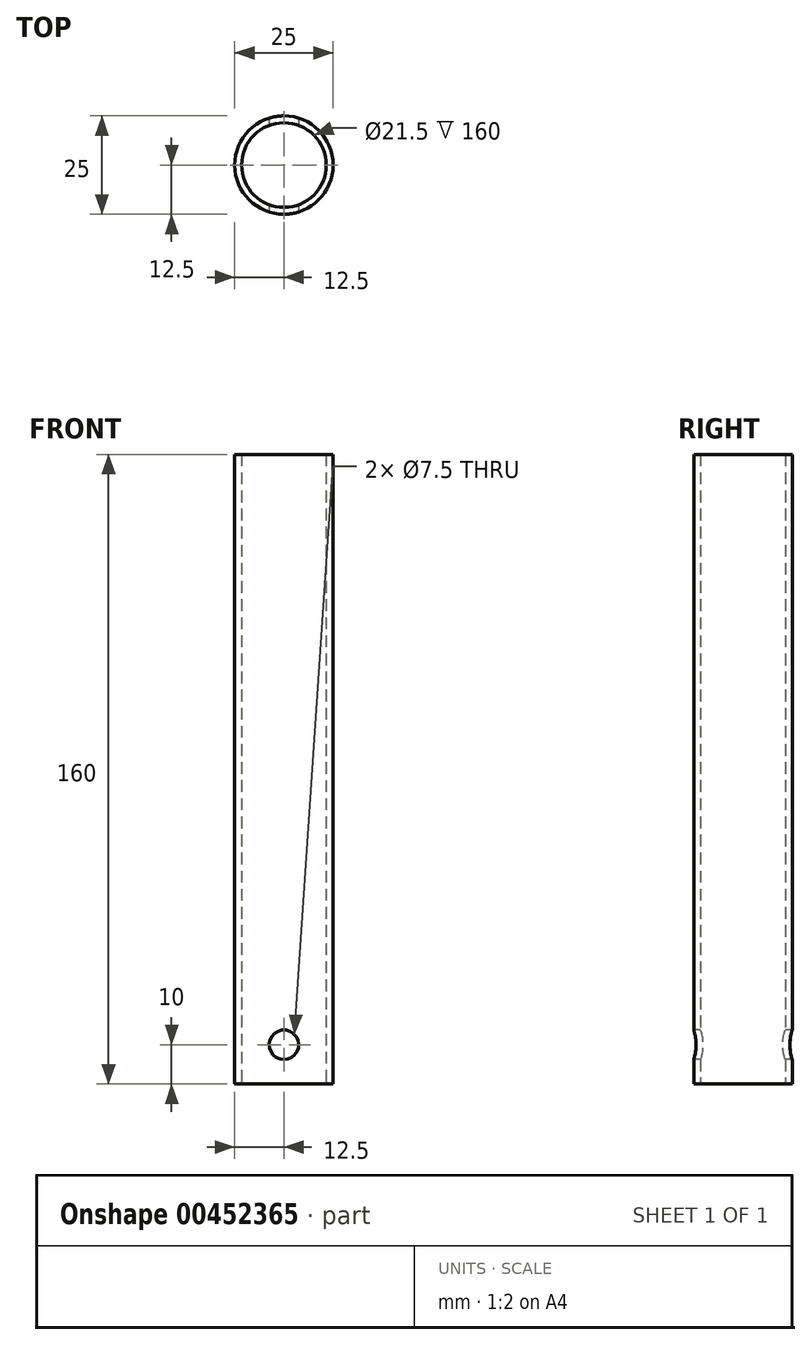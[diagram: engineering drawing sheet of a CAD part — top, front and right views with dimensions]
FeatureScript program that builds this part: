
annotation { "Feature Type Name" : "Feature", "Feature Type Description" : "" }
export const myFeature = defineFeature(function(context is Context, id is Id, definition is map)
    precondition{}
    {
        {
            var Q0;
            Q0=qCreatedBy(makeId("Top.planeOp"),FACE);
            var sketch = newSketch(context, id + "F0", { "sketchPlane" : qUnion([Q0])});
            skCircle(sketch, "E0", {"center": v(0, 0) * mm, "radius": 10.75 * mm});
            skCircle(sketch, "E1", {"center": v(0, 0) * mm, "radius": 12.5 * mm});
            skSolve(sketch);
        }
        {
            var Q0;
            Q0 = qSketchRegion(id + "F0", true);
            extrude(context, id + "F1", {"entities" : qUnion([Q0]), "depth" : 160 * mm});
        }
        {
            var Q0;
            Q0=qCreatedBy(makeId("Front.planeOp"),FACE);
            var sketch = newSketch(context, id + "F2", { "sketchPlane" : qUnion([Q0])});
            skCircle(sketch, "E2", {"center": v(0, 10) * mm, "radius": 3.75 * mm});
            skSolve(sketch);
        }
        {
            var Q0;
            Q0 = qSketchRegion(id + "F2", true);
            extrude(context, id + "F3", {"entities" : qUnion([Q0]), "operationType" : NewBodyOperationType.REMOVE, "endBound" : BoundingType.SYMMETRIC, "oppositeDirection" : true, "depth" : 25 * mm});
        }
    });
